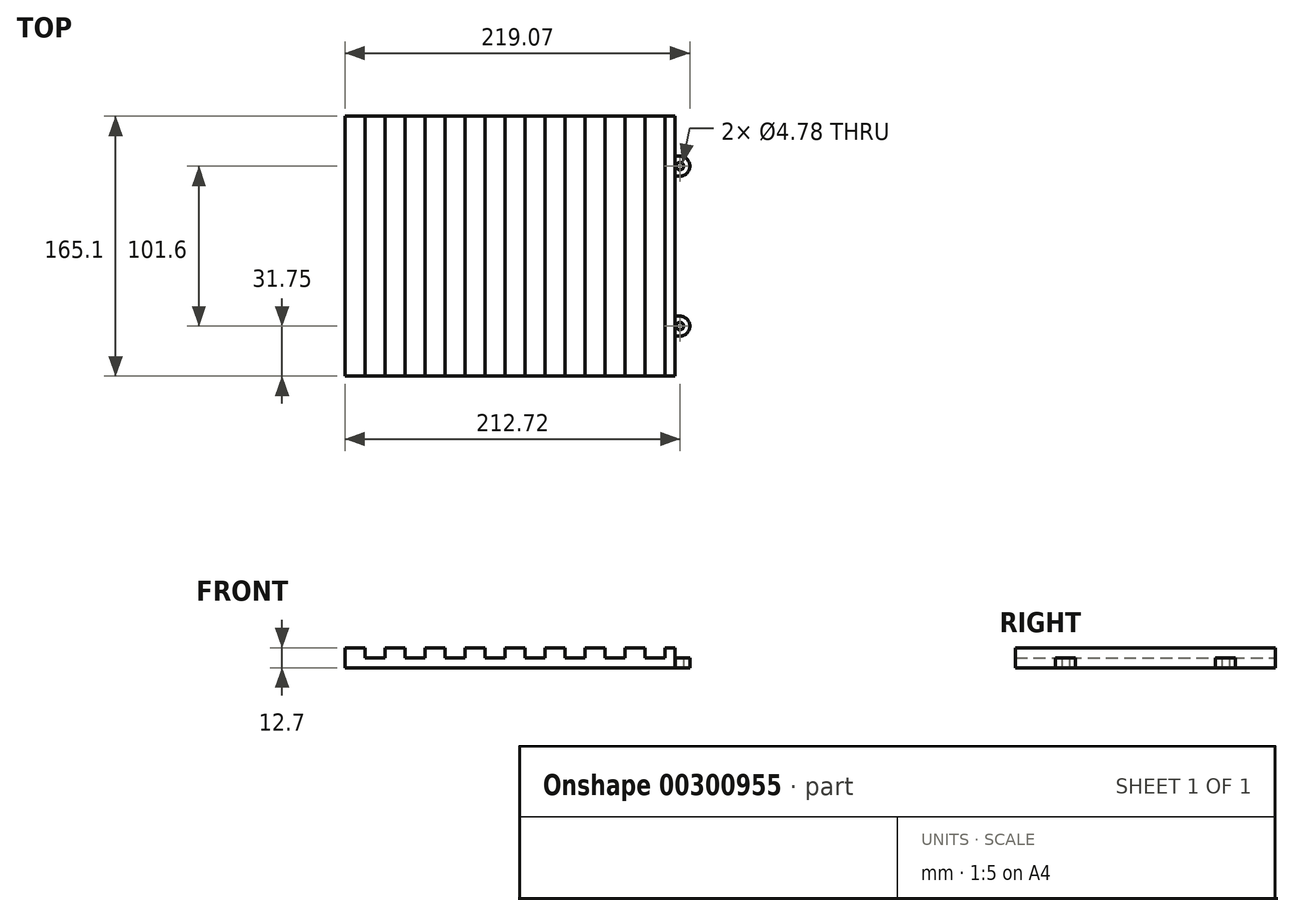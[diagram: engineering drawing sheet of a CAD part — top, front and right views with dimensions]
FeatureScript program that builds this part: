
annotation { "Feature Type Name" : "Feature", "Feature Type Description" : "" }
export const myFeature = defineFeature(function(context is Context, id is Id, definition is map)
    precondition{}
    {
        {
            var Q0;
            Q0=qCreatedBy(makeId("Front.planeOp"),FACE);
            var sketch = newSketch(context, id + "F0", { "sketchPlane" : qUnion([Q0])});
            skLineSegment(sketch, "E0.bottom", {"start": v(-104.78, 0) * mm, "end": v(104.78, 0) * mm});
            skLineSegment(sketch, "E0.top", {"start": v(-104.78, 12.7) * mm, "end": v(-92.08, 12.7) * mm});
            skLineSegment(sketch, "E0.left", {"start": v(-104.78, 0) * mm, "end": v(-104.78, 12.7) * mm});
            skLineSegment(sketch, "E0.right", {"start": v(104.78, 0) * mm, "end": v(104.78, 12.7) * mm});
            skLineSegment(sketch, "E1", {"start": v(-92.08, 12.7) * mm, "end": v(-92.08, 6.35) * mm});
            skLineSegment(sketch, "E2", {"start": v(-92.08, 6.35) * mm, "end": v(-79.38, 6.35) * mm});
            skLineSegment(sketch, "E3", {"start": v(-79.38, 6.35) * mm, "end": v(-79.38, 12.7) * mm});
            skLineSegment(sketch, "E4.trimOffspring", {"start": v(-79.38, 12.7) * mm, "end": v(-66.68, 12.7) * mm});
            skLineSegment(sketch, "E5.1.0.0", {"start": v(-66.68, 12.7) * mm, "end": v(-66.68, 6.35) * mm});
            skLineSegment(sketch, "E5.1.0.1", {"start": v(-66.68, 6.35) * mm, "end": v(-53.98, 6.35) * mm});
            skLineSegment(sketch, "E5.1.0.2", {"start": v(-53.98, 6.35) * mm, "end": v(-53.98, 12.7) * mm});
            skLineSegment(sketch, "E5.2.0.0", {"start": v(-41.28, 12.7) * mm, "end": v(-41.28, 6.35) * mm});
            skLineSegment(sketch, "E5.2.0.1", {"start": v(-41.28, 6.35) * mm, "end": v(-28.58, 6.35) * mm});
            skLineSegment(sketch, "E5.2.0.2", {"start": v(-28.58, 6.35) * mm, "end": v(-28.58, 12.7) * mm});
            skLineSegment(sketch, "E5.3.0.0", {"start": v(-15.88, 12.7) * mm, "end": v(-15.88, 6.35) * mm});
            skLineSegment(sketch, "E5.3.0.1", {"start": v(-15.88, 6.35) * mm, "end": v(-3.18, 6.35) * mm});
            skLineSegment(sketch, "E5.3.0.2", {"start": v(-3.18, 6.35) * mm, "end": v(-3.18, 12.7) * mm});
            skLineSegment(sketch, "E5.4.0.0", {"start": v(9.52, 12.7) * mm, "end": v(9.52, 6.35) * mm});
            skLineSegment(sketch, "E5.4.0.1", {"start": v(9.52, 6.35) * mm, "end": v(22.22, 6.35) * mm});
            skLineSegment(sketch, "E5.4.0.2", {"start": v(22.22, 6.35) * mm, "end": v(22.22, 12.7) * mm});
            skLineSegment(sketch, "E5.5.0.0", {"start": v(34.92, 12.7) * mm, "end": v(34.92, 6.35) * mm});
            skLineSegment(sketch, "E5.5.0.1", {"start": v(34.92, 6.35) * mm, "end": v(47.62, 6.35) * mm});
            skLineSegment(sketch, "E5.5.0.2", {"start": v(47.62, 6.35) * mm, "end": v(47.62, 12.7) * mm});
            skLineSegment(sketch, "E5.6.0.0", {"start": v(60.32, 12.7) * mm, "end": v(60.32, 6.35) * mm});
            skLineSegment(sketch, "E5.6.0.1", {"start": v(60.32, 6.35) * mm, "end": v(73.02, 6.35) * mm});
            skLineSegment(sketch, "E5.6.0.2", {"start": v(73.02, 6.35) * mm, "end": v(73.02, 12.7) * mm});
            skLineSegment(sketch, "E5.direction1", {"start": v(-92.08, 6.35) * mm, "end": v(-66.68, 6.35) * mm, "construction": true});
            skLineSegment(sketch, "E6.trimOffspring", {"start": v(-53.98, 12.7) * mm, "end": v(-41.28, 12.7) * mm});
            skLineSegment(sketch, "E7.trimOffspring", {"start": v(-28.58, 12.7) * mm, "end": v(-15.88, 12.7) * mm});
            skLineSegment(sketch, "E8.trimOffspring", {"start": v(-3.18, 12.7) * mm, "end": v(9.52, 12.7) * mm});
            skLineSegment(sketch, "E9.trimOffspring", {"start": v(22.22, 12.7) * mm, "end": v(34.92, 12.7) * mm});
            skLineSegment(sketch, "E10.trimOffspring", {"start": v(47.62, 12.7) * mm, "end": v(60.32, 12.7) * mm});
            skLineSegment(sketch, "E11.trimOffspring", {"start": v(73.02, 12.7) * mm, "end": v(85.72, 12.7) * mm});
            skLineSegment(sketch, "E12.trimOffspring", {"start": v(98.42, 12.7) * mm, "end": v(104.78, 12.7) * mm});
            skLineSegment(sketch, "E13.0.7.0", {"start": v(85.72, 12.7) * mm, "end": v(85.72, 6.35) * mm});
            skLineSegment(sketch, "E13.3.7.0", {"start": v(85.72, 6.35) * mm, "end": v(98.42, 6.35) * mm});
            skLineSegment(sketch, "E13.6.7.0", {"start": v(98.42, 6.35) * mm, "end": v(98.42, 12.7) * mm});
            skSolve(sketch);
        }
        {
            var Q0;
            Q0 = qSketchRegion(id + "F0", true);
            extrude(context, id + "F1", {"entities" : qUnion([Q0]), "depth" : 165.1 * mm});
        }
        {
            var Q0;
            Q0=makeQuery(id+"F1.opExtrude","SWEPT_FACE",FACE,{"disambiguationData":[OSD([sQuery(id+"F0.wireOp",EDGE,"E0.bottom")])]});
            var sketch = newSketch(context, id + "F2", { "sketchPlane" : qUnion([Q0])});
            skLineSegment(sketch, "E14.bottom", {"start": v(104.78, 139.7) * mm, "end": v(107.95, 139.7) * mm});
            skLineSegment(sketch, "E14.top", {"start": v(104.78, 127) * mm, "end": v(107.95, 127) * mm});
            skLineSegment(sketch, "E14.left", {"start": v(104.78, 139.7) * mm, "end": v(104.78, 127) * mm});
            skArc(sketch, "E15", {"start": v(107.95, 127) * mm, "mid": v(114.3, 133.35) * mm, "end": v(107.95, 139.7) * mm});
            skCircle(sketch, "E16", {"center": v(107.95, 133.35) * mm, "radius": 2.39 * mm});
            skLineSegment(sketch, "E17", {"start": v(-104.78, 82.55) * mm, "end": v(104.78, 82.55) * mm, "construction": true});
            skCircle(sketch, "E18.MirrorC", {"center": v(107.95, 31.75) * mm, "radius": 2.39 * mm});
            skArc(sketch, "E19.MirrorCS", {"start": v(107.95, 38.1) * mm, "mid": v(114.3, 31.75) * mm, "end": v(107.95, 25.4) * mm});
            skLineSegment(sketch, "E20.MirrorCS", {"start": v(104.78, 25.4) * mm, "end": v(104.78, 38.1) * mm});
            skLineSegment(sketch, "E21.MirrorCS", {"start": v(104.78, 38.1) * mm, "end": v(107.95, 38.1) * mm});
            skLineSegment(sketch, "E22.MirrorCS", {"start": v(104.78, 25.4) * mm, "end": v(107.95, 25.4) * mm});
            skSolve(sketch);
        }
        {
            var Q0;
            Q0 = qSketchRegion(id + "F2", true);
            extrude(context, id + "F3", {"entities" : qUnion([Q0]), "operationType" : NewBodyOperationType.ADD, "oppositeDirection" : true, "depth" : 6.35 * mm});
        }
        {
            var Q0;
            Q0=qCreatedBy(makeId("Right.planeOp"),FACE);
            cPlane(context, id + "F4", {"entities" : qUnion([Q0]), "cplaneType" : CPlaneType.OFFSET, "offset" : 101.6 * mm, "width" : 152.4 * mm, "height" : 152.4 * mm});
        }
    });
